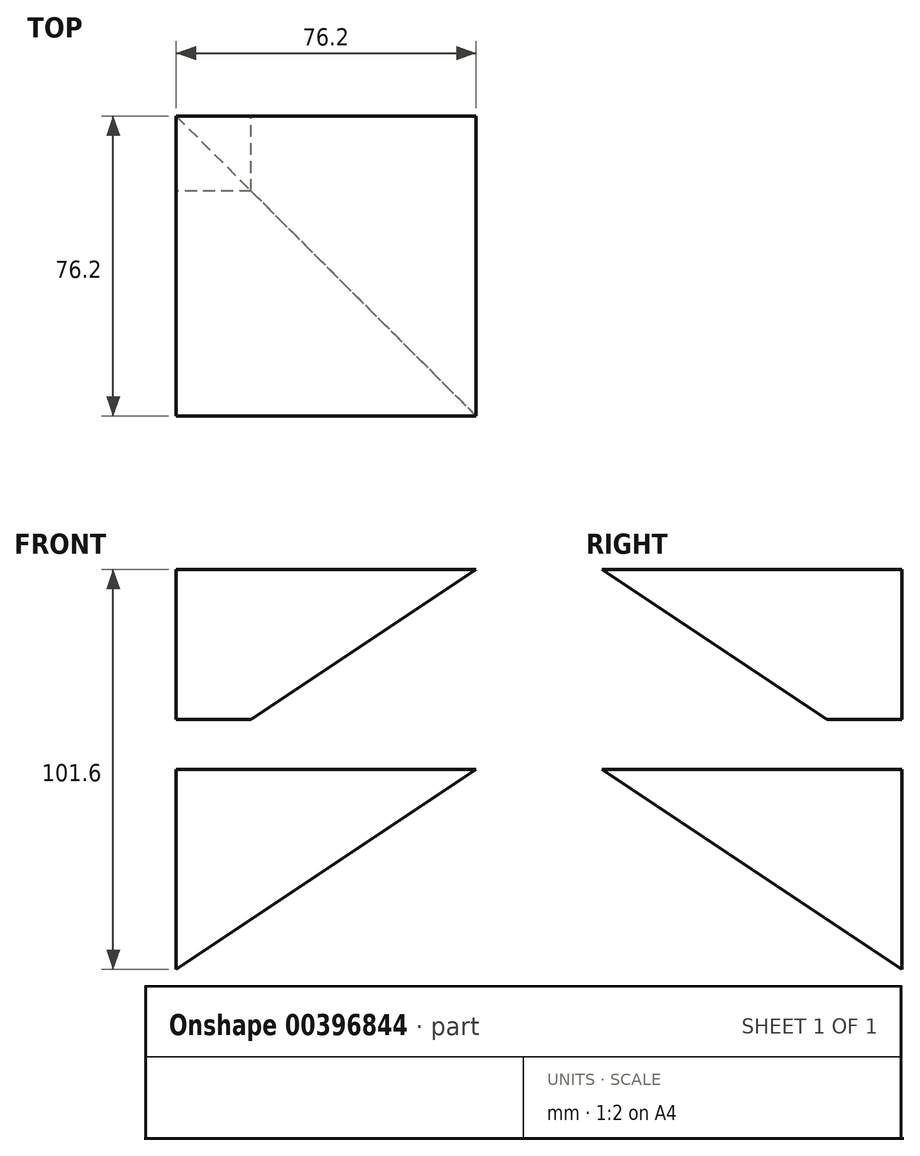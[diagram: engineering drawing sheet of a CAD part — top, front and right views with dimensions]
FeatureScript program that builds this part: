
annotation { "Feature Type Name" : "Feature", "Feature Type Description" : "" }
export const myFeature = defineFeature(function(context is Context, id is Id, definition is map)
    precondition{}
    {
        {
            assignVariable(context, id + "F0", {"name" : "x", "anyValue" : 25.4 * mm});
        }
        {
            var Q0;
            Q0=qCreatedBy(makeId("Front.planeOp"),FACE);
            var sketch = newSketch(context, id + "F1", { "sketchPlane" : qUnion([Q0])});
            skLineSegment(sketch, "E0.bottom", {"start": v(0, 0) * mm, "end": v(76.2, 0) * mm, "construction": true});
            skLineSegment(sketch, "E0.top", {"start": v(0, 50.8) * mm, "end": v(76.2, 50.8) * mm, "construction": true});
            skLineSegment(sketch, "E0.left", {"start": v(0, 0) * mm, "end": v(0, 50.8) * mm, "construction": true});
            skLineSegment(sketch, "E0.right", {"start": v(76.2, 0) * mm, "end": v(76.2, 50.8) * mm, "construction": true});
            skLineSegment(sketch, "E1", {"start": v(0, 0) * mm, "end": v(19.05, 12.7) * mm, "construction": true});
            skLineSegment(sketch, "E2", {"start": v(76.2, 50.8) * mm, "end": v(0, 50.8) * mm});
            skLineSegment(sketch, "E3", {"start": v(0, 50.8) * mm, "end": v(0, 12.7) * mm});
            skLineSegment(sketch, "E4.bottom", {"start": v(0, -50.8) * mm, "end": v(76.2, -50.8) * mm, "construction": true});
            skLineSegment(sketch, "E4.left", {"start": v(0, -50.8) * mm, "end": v(0, 0) * mm, "construction": true});
            skLineSegment(sketch, "E4.right", {"start": v(76.2, -50.8) * mm, "end": v(76.2, 0) * mm, "construction": true});
            skLineSegment(sketch, "E5", {"start": v(0, -50.8) * mm, "end": v(76.2, 0) * mm});
            skLineSegment(sketch, "E6", {"start": v(76.2, 0) * mm, "end": v(0, 0) * mm});
            skLineSegment(sketch, "E7", {"start": v(0, 0) * mm, "end": v(0, -50.8) * mm});
            skLineSegment(sketch, "E8", {"start": v(19.05, 12.7) * mm, "end": v(0, 12.7) * mm});
            skLineSegment(sketch, "E9", {"start": v(19.05, 12.7) * mm, "end": v(76.2, 50.8) * mm});
            skSolve(sketch);
        }
        {
            var Q0;
            Q0=makeQuery(id+"F1.imprint","IMPRINT",FACE,{"disambiguationData":[TD([[makeQuery(id+"F1.imprint","IMPRINT",EDGE,{"derivedFrom":sQuery(id+"F1.wireOp",EDGE,"E2")}),1.0]])]});
            var Q1;
            Q1=makeQuery(id+"F1.imprint","IMPRINT",FACE,{"disambiguationData":[TD([[makeQuery(id+"F1.imprint","IMPRINT",EDGE,{"derivedFrom":sQuery(id+"F1.wireOp",EDGE,"E5")}),1.0]])]});
            extrude(context, id + "F2", {"entities" : qUnion([Q0, Q1]), "depth" : 3 * getVariable(context, 'x')});
        }
        {
            var Q0;
            Q0=qCreatedBy(makeId("Right.planeOp"),FACE);
            var sketch = newSketch(context, id + "F3", { "sketchPlane" : qUnion([Q0])});
            skLineSegment(sketch, "E10", {"start": v(0, -50.8) * mm, "end": v(-76.2, 0) * mm});
            skLineSegment(sketch, "E11", {"start": v(-76.2, 50.8) * mm, "end": v(-19.05, 12.7) * mm});
            skLineSegment(sketch, "E12", {"start": v(-76.2, 50.8) * mm, "end": v(-76.2, 12.7) * mm});
            skLineSegment(sketch, "E13", {"start": v(-76.2, 12.7) * mm, "end": v(-19.05, 12.7) * mm});
            skLineSegment(sketch, "E14", {"start": v(-76.2, 0) * mm, "end": v(-76.2, -50.8) * mm});
            skLineSegment(sketch, "E15", {"start": v(-76.2, -50.8) * mm, "end": v(0, -50.8) * mm});
            skSolve(sketch);
        }
        {
            var Q0;
            Q0=makeQuery(id+"F3.imprint","IMPRINT",FACE,{"disambiguationData":[TD([[makeQuery(id+"F3.imprint","IMPRINT",EDGE,{"derivedFrom":sQuery(id+"F3.wireOp",EDGE,"E11")}),-1.0]])]});
            var Q1;
            Q1=makeQuery(id+"F3.imprint","IMPRINT",FACE,{"disambiguationData":[TD([[makeQuery(id+"F3.imprint","IMPRINT",EDGE,{"derivedFrom":sQuery(id+"F3.wireOp",EDGE,"E10")}),1.0]])]});
            extrude(context, id + "F4", {"entities" : qUnion([Q0, Q1]), "operationType" : NewBodyOperationType.REMOVE, "endBound" : BoundingType.THROUGH_ALL, "depth" : 25.4 * mm});
        }
    });
